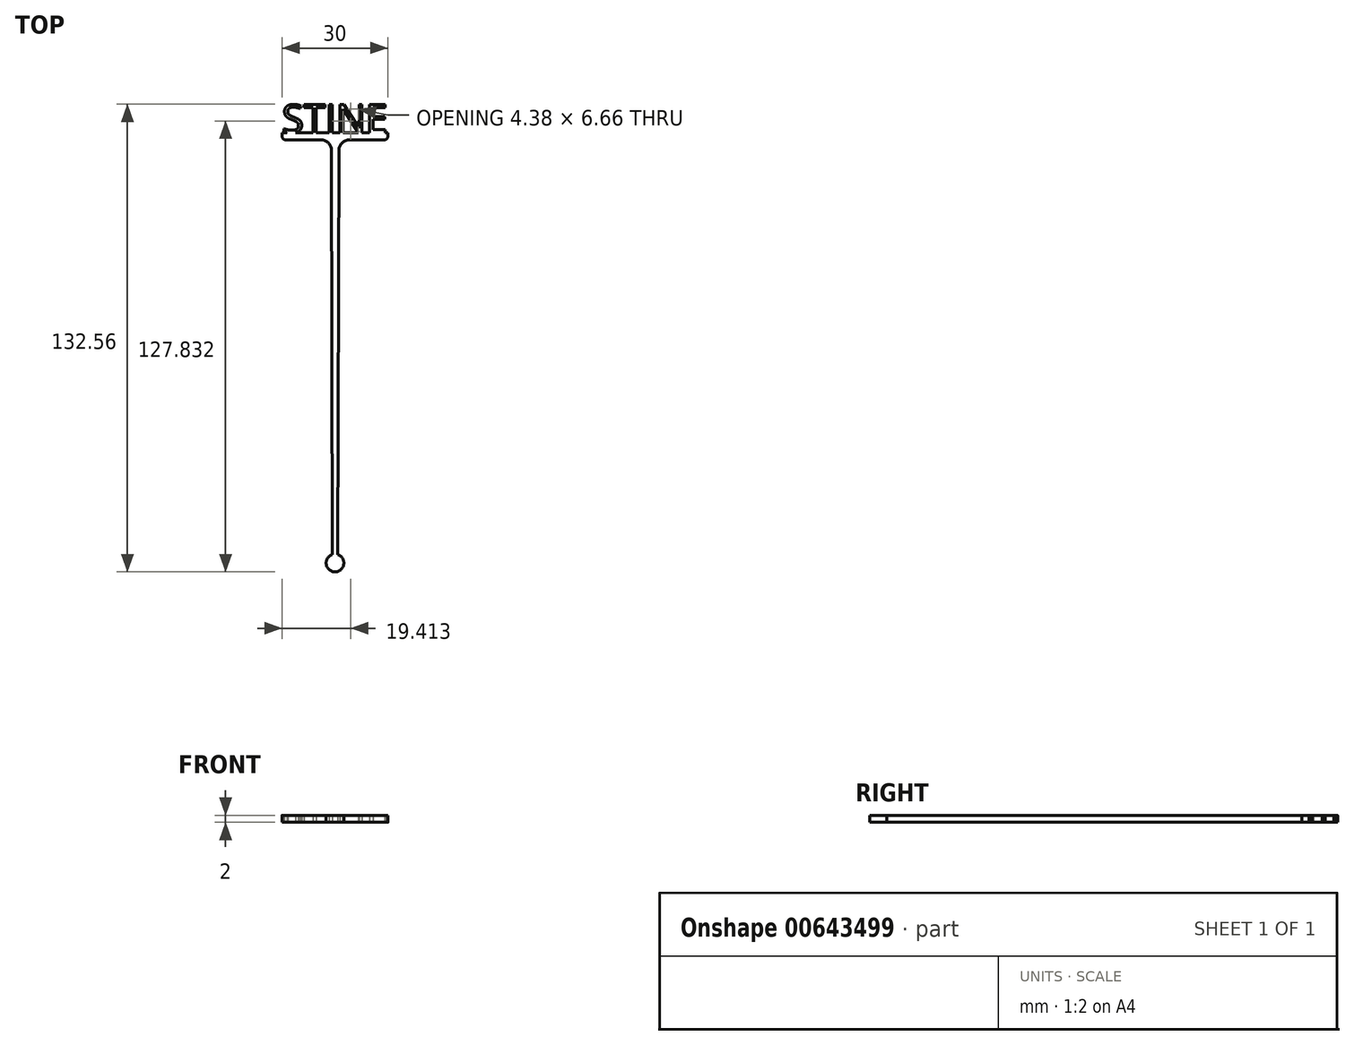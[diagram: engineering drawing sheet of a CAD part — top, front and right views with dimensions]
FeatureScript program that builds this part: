
annotation { "Feature Type Name" : "Feature", "Feature Type Description" : "" }
export const myFeature = defineFeature(function(context is Context, id is Id, definition is map)
    precondition{}
    {
        {
            var Q0;
            Q0=qCreatedBy(makeId("Top.planeOp"),FACE);
            var sketch = newSketch(context, id + "F0", { "sketchPlane" : qUnion([Q0])});
            skText(sketch, "E0", { "text": "STINE", "fontName": "OpenSans-Regular.ttf"});
            skLineSegment(sketch, "E1.bottom", {"start": v(-15, 0) * mm, "end": v(15, 0) * mm});
            skLineSegment(sketch, "E1.top", {"start": v(-14, -2) * mm, "end": v(-4, -2) * mm});
            skLineSegment(sketch, "E1.left", {"start": v(-15, 0) * mm, "end": v(-15, -1) * mm});
            skLineSegment(sketch, "E1.right", {"start": v(15, 0) * mm, "end": v(15, -1) * mm});
            skLineSegment(sketch, "E2.bottom", {"start": v(-1, -2) * mm, "end": v(1, -2) * mm});
            skLineSegment(sketch, "E3", {"start": v(0, -2) * mm, "end": v(0, -122) * mm, "construction": true});
            skPoint(sketch, "E3.endSnap0", {"position": v(0, -2) * mm});
            skCircle(sketch, "E4", {"center": v(0, -122) * mm, "radius": 2.5 * mm});
            skLineSegment(sketch, "E5", {"start": v(-0.75, -122) * mm, "end": v(0.75, -122) * mm, "construction": true});
            skLineSegment(sketch, "E6", {"start": v(-1, -5) * mm, "end": v(-0.75, -122) * mm});
            skLineSegment(sketch, "E7", {"start": v(0.75, -122) * mm, "end": v(1.14, -5) * mm});
            skLineSegment(sketch, "E8", {"start": v(4.14, -2) * mm, "end": v(14, -2) * mm});
            skArc(sketch, "E9.filletArc", {"start": v(4.14, -2) * mm, "mid": v(2.02, -2.88) * mm, "end": v(1.14, -5) * mm});
            skPoint(sketch, "E10.newPointB", {"position": v(-1, -2) * mm});
            skArc(sketch, "E10.filletArc", {"start": v(-1, -5) * mm, "mid": v(-1.87, -2.88) * mm, "end": v(-4, -2) * mm});
            skPoint(sketch, "E11.visualSharp", {"position": v(-15, -2) * mm});
            skArc(sketch, "E11.filletArc", {"start": v(-15, -1) * mm, "mid": v(-14.7, -1.7) * mm, "end": v(-14, -2) * mm});
            skPoint(sketch, "E12.visualSharp", {"position": v(15, -2) * mm});
            skArc(sketch, "E12.filletArc", {"start": v(14, -2) * mm, "mid": v(14.7, -1.7) * mm, "end": v(15, -1) * mm});
            const initialGuessF0  = {"E0": [-0.015, 0, 1, 0, 0.00801]};
            skSetInitialGuess(sketch, initialGuessF0);
            skSolve(sketch);
        }
        {
            var Q0;
            Q0 = qSketchRegion(id + "F0", true);
            extrude(context, id + "F1", {"entities" : qUnion([Q0]), "depth" : 2 * mm, "offsetDistance" : 25 * mm});
        }
    });
